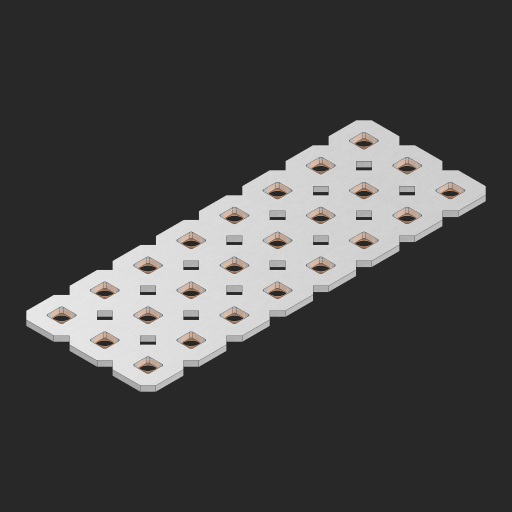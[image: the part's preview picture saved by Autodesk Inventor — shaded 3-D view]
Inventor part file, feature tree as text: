
AUTODESK INVENTOR PART (.ipt)
format: ipt  version: 2023 (Build 270158000, 158)  size: 571,904 bytes
history: native  units: in
note: dims shown in document units (in); Inventor stores cm internally (conversion verified against a paired STEP export)
features: other x25, extrude x23, sketch x2, pattern_linear x1
ambient origin geometry x8: Origin, YZ Plane, XZ Plane, XY Plane, X Axis, Y Axis, Z Axis, Center Point
bodies: Solid1 (feature_tree), Body (feature_tree)
feature tree (51):
  pattern_linear  "Rectangular Pattern1"  Spacing1=0.09in  [1 undecoded]
  sketch  "Sketch1"  dims[d1=0.5in]
  sketch  "Sketch2"  dims[d2=0.182in d3=0.09in d4=0.09in d5=0.09in d6=0.09in d7=0.09in d8=0.09in d9=0.09in d10=0.09in d11=0.02in d13=0.0in d14=0.172in d15=0.0625in d16=0.0in d19=0.5in d22=0.5in]
  other  "Srf1"
  other  "Srf126"
  other  "Srf127"
  other  "Srf128"
  other  "Srf129"
  other  "Srf130"
  other  "Srf131"
  other  "Srf250"
  other  "Srf268"
  other  "Srf269"
  other  "Srf270"
  other  "Srf271"
  other  "Srf272"
  other  "Srf273"
  other  "Srf274"
  other  "Srf275"
  other  "Srf293"
  other  "Srf294"
  other  "Srf295"
  other  "Srf296"
  other  "Srf297"
  other  "Srf298"
  other  "Srf299"
  other  "Srf300"
  other  "Circle"
  extrude  "ExtrusionSrf126"  Depth=0.09in
  extrude  "ExtrusionSrf127"  Depth=0.09in
  extrude  "ExtrusionSrf128"  Depth=0.09in
  extrude  "ExtrusionSrf129"  Depth=0.09in
  extrude  "ExtrusionSrf130"  Depth=0.09in
  extrude  "ExtrusionSrf131"  Depth=0.09in
  extrude  "ExtrusionSrf250"  Depth=0.09in
  extrude  "ExtrusionSrf268"  Depth=0.02in
  extrude  "ExtrusionSrf269"  TaperAngle=0.0deg  [1 undecoded]
  extrude  "ExtrusionSrf270"  Depth=0.5in
  extrude  "ExtrusionSrf271"  Depth=0.0625in TaperAngle=0.0deg
  extrude  "ExtrusionSrf272"  Depth=0.5in
  extrude  "ExtrusionSrf273"  Depth=0.5in
  extrude  "ExtrusionSrf274"  [1 undecoded]
  extrude  "ExtrusionSrf275"  [1 undecoded]
  extrude  "ExtrusionSrf293"  [1 undecoded]
  extrude  "ExtrusionSrf294"  [1 undecoded]
  extrude  "ExtrusionSrf295"  [1 undecoded]
  extrude  "ExtrusionSrf296"  [1 undecoded]
  extrude  "ExtrusionSrf297"  [1 undecoded]
  extrude  "ExtrusionSrf298"  [1 undecoded]
  extrude  "ExtrusionSrf299"  [1 undecoded]
  extrude  "ExtrusionSrf300"  [1 undecoded]
note: 12 required parameter values undecoded (feature->parameter linkage not recoverable at this tier; creation-order binding heuristic only, values carry confidence <= 0.55)
